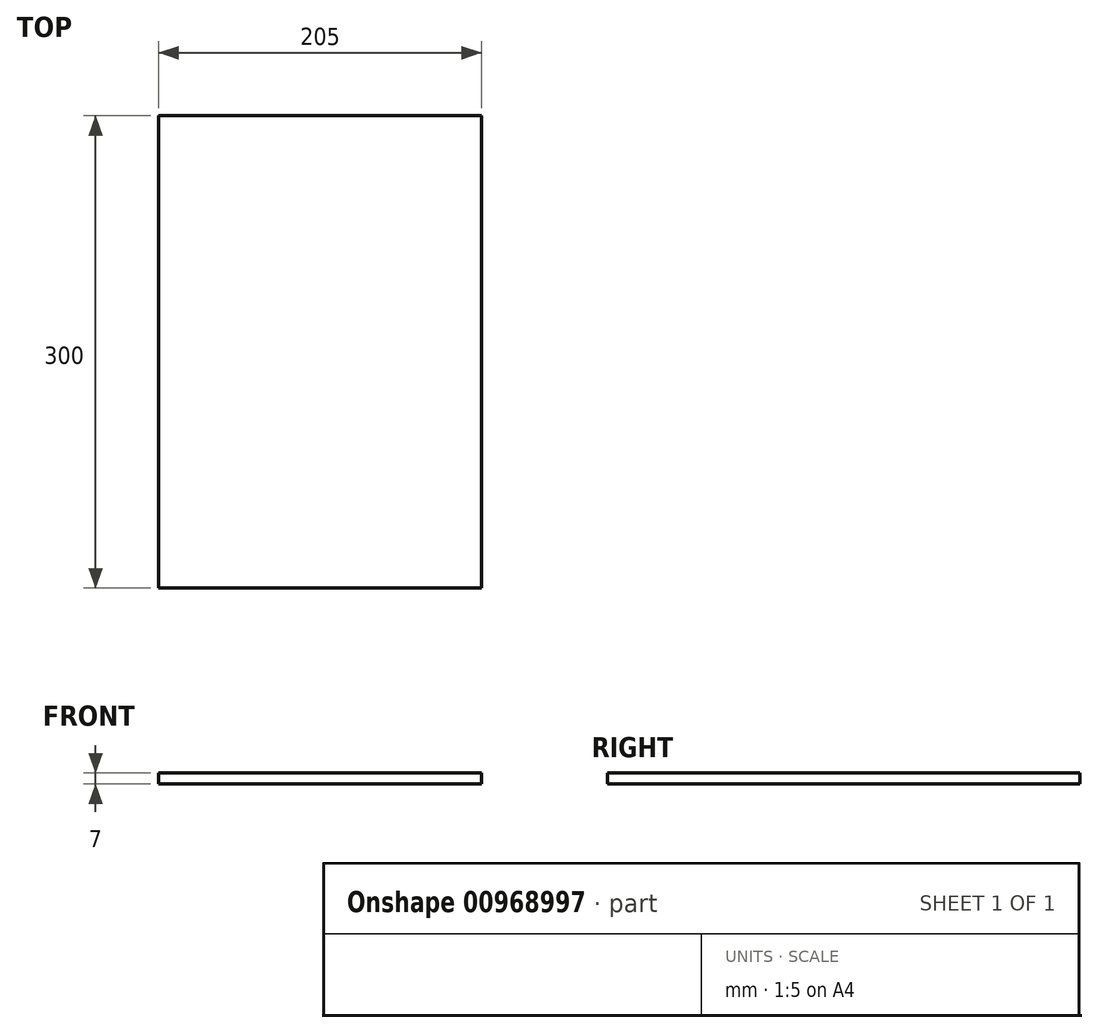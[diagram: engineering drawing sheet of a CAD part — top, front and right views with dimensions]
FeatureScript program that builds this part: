
annotation { "Feature Type Name" : "Feature", "Feature Type Description" : "" }
export const myFeature = defineFeature(function(context is Context, id is Id, definition is map)
    precondition{}
    {
        {
            var Q0;
            Q0=qCreatedBy(makeId("Top.planeOp"),FACE);
            var sketch = newSketch(context, id + "F0", { "sketchPlane" : qUnion([Q0])});
            skLineSegment(sketch, "E0.bottom", {"start": v(102.5, 150) * mm, "end": v(-102.5, 150) * mm});
            skLineSegment(sketch, "E0.top", {"start": v(102.5, -150) * mm, "end": v(-102.5, -150) * mm});
            skLineSegment(sketch, "E0.left", {"start": v(102.5, 150) * mm, "end": v(102.5, -150) * mm});
            skLineSegment(sketch, "E0.right", {"start": v(-102.5, 150) * mm, "end": v(-102.5, -150) * mm});
            skPoint(sketch, "E0.middle", {"position": v(0, 0) * mm});
            skSolve(sketch);
        }
        {
            var Q0;
            Q0=makeQuery(id+"F0.imprint","IMPRINT",FACE,{"disambiguationData":[TD([[makeQuery(id+"F0.imprint","IMPRINT",EDGE,{"derivedFrom":sQuery(id+"F0.wireOp",EDGE,"E0.bottom")}),1.0]])]});
            extrude(context, id + "F1", {"entities" : qUnion([Q0]), "depth" : 7 * mm, "offsetDistance" : 25 * mm});
        }
    });
